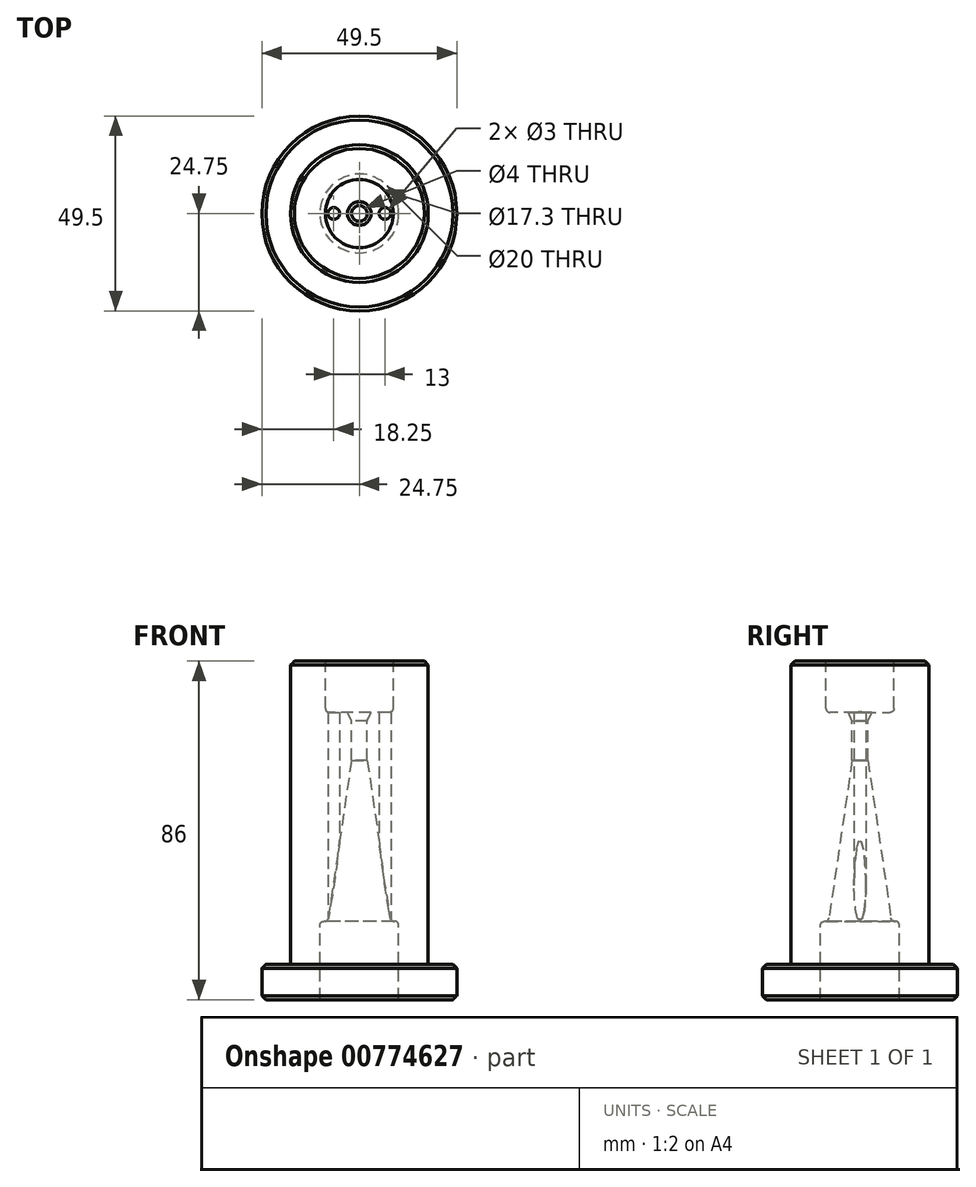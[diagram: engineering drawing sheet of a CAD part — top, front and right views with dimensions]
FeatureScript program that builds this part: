
annotation { "Feature Type Name" : "Feature", "Feature Type Description" : "" }
export const myFeature = defineFeature(function(context is Context, id is Id, definition is map)
    precondition{}
    {
        {
            var Q0;
            Q0=qCreatedBy(makeId("Front.planeOp"),FACE);
            var sketch = newSketch(context, id + "F0", { "sketchPlane" : qUnion([Q0])});
            skLineSegment(sketch, "E0", {"start": v(0, 0) * mm, "end": v(-10, 0) * mm});
            skLineSegment(sketch, "E1", {"start": v(-10, -2) * mm, "end": v(-10, -20) * mm});
            skLineSegment(sketch, "E2", {"start": v(-10, -20) * mm, "end": v(-24.75, -20) * mm});
            skLineSegment(sketch, "E3", {"start": v(-24.75, -20) * mm, "end": v(-24.75, -11) * mm});
            skLineSegment(sketch, "E4", {"start": v(-24.75, -11) * mm, "end": v(-18, -11) * mm});
            skLineSegment(sketch, "E5", {"start": v(-17.5, -10.5) * mm, "end": v(-17.5, 66) * mm});
            skLineSegment(sketch, "E6", {"start": v(-17.5, 66) * mm, "end": v(-8.65, 66) * mm});
            skLineSegment(sketch, "E7", {"start": v(-7.65, 53) * mm, "end": v(-3, 53) * mm});
            skLineSegment(sketch, "E8", {"start": v(-8.65, 54) * mm, "end": v(-8.65, 66) * mm});
            skLineSegment(sketch, "E9", {"start": v(-3, 53) * mm, "end": v(-2, 50.86) * mm});
            skLineSegment(sketch, "E10", {"start": v(-2, 50.86) * mm, "end": v(-2, 40.84) * mm});
            skPoint(sketch, "E11.orphan", {"position": v(0, 53) * mm});
            skLineSegment(sketch, "E12", {"start": v(-8, 0) * mm, "end": v(-8, 0) * mm});
            skLineSegment(sketch, "E13", {"start": v(-7.9, 0.72) * mm, "end": v(-2, 40.84) * mm});
            skPoint(sketch, "E14.end.orphan", {"position": v(0, 66) * mm});
            skPoint(sketch, "E15.visualSharp", {"position": v(-10, 0) * mm});
            skPoint(sketch, "E16.visualSharp", {"position": v(-8, 0) * mm});
            skArc(sketch, "E16.filletArc", {"start": v(-8.59, -0.09) * mm, "mid": v(-8.12, 0.22) * mm, "end": v(-7.9, 0.72) * mm});
            skLineSegment(sketch, "E17", {"start": v(-8.59, -0.09) * mm, "end": v(-8.94, -0.07) * mm});
            skLineSegment(sketch, "E18", {"start": v(-10, -2) * mm, "end": v(-10, -1.06) * mm});
            skArc(sketch, "E19.filletArc", {"start": v(-8.94, -0.07) * mm, "mid": v(-9.68, -0.34) * mm, "end": v(-10, -1.06) * mm});
            skPoint(sketch, "E20.visualSharp", {"position": v(-17.5, -11) * mm});
            skArc(sketch, "E20.filletArc", {"start": v(-18, -11) * mm, "mid": v(-17.65, -10.85) * mm, "end": v(-17.5, -10.5) * mm});
            skLineSegment(sketch, "E21", {"start": v(0, 75.07) * mm, "end": v(0, -45.35) * mm});
            skPoint(sketch, "E22.visualSharp", {"position": v(-8.65, 53) * mm});
            skArc(sketch, "E22.filletArc", {"start": v(-8.65, 54) * mm, "mid": v(-8.36, 53.3) * mm, "end": v(-7.65, 53) * mm});
            skSolve(sketch);
        }
        {
            var Q0;
            Q0=makeQuery(id+"F0.imprint","IMPRINT",FACE,{"disambiguationData":[TD([[makeQuery(id+"F0.imprint","IMPRINT",EDGE,{"derivedFrom":sQuery(id+"F0.wireOp",EDGE,"E1")}),-1.0]])]});
            var Q1;
            Q1=sQuery(id+"F0.wireOp",EDGE,"E21");
            revolve(context, id + "F1", {"surfaceOperationType" : NewSurfaceOperationType.NEW, "entities" : qUnion([Q0]), "axis" : qUnion([Q1]), "revolveType" : RevolveType.FULL});
        }
        {
            var Q0;
            Q0=makeQuery(id+"F1.opRevolve","SWEPT_EDGE",EDGE,{"disambiguationData":[OSD([sQuery(id+"F0.wireOp",EDGE,"E3"),sQuery(id+"F0.wireOp",EDGE,"E4")])]});
            var Q1;
            Q1=makeQuery(id+"F1.opRevolve","SWEPT_EDGE",EDGE,{"disambiguationData":[OSD([sQuery(id+"F0.wireOp",EDGE,"E5"),sQuery(id+"F0.wireOp",EDGE,"E6")])]});
            var Q2;
            Q2=makeQuery(id+"F1.opRevolve","SWEPT_EDGE",EDGE,{"disambiguationData":[OSD([sQuery(id+"F0.wireOp",EDGE,"E2"),sQuery(id+"F0.wireOp",EDGE,"E3")])]});
            chamfer(context, id + "F2", {"entities" : qUnion([Q0, Q1, Q2]), "width" : 1 * mm, "tangentPropagation" : true});
        }
        {
            var Q0;
            Q0=qCreatedBy(makeId("Top.planeOp"),FACE);
            var sketch = newSketch(context, id + "F3", { "sketchPlane" : qUnion([Q0])});
            skLineSegment(sketch, "E23", {"start": v(0, 0) * mm, "end": v(6.5, 0) * mm});
            skLineSegment(sketch, "E24", {"start": v(0, 0) * mm, "end": v(-6.5, 0) * mm});
            skCircle(sketch, "E25", {"center": v(-6.5, 0) * mm, "radius": 1.5 * mm});
            skCircle(sketch, "E26", {"center": v(6.5, 0) * mm, "radius": 1.5 * mm});
            skSolve(sketch);
        }
        {
            var Q0;
            Q0=makeQuery(id+"F3.imprint","IMPRINT",FACE,{"disambiguationData":[TD([[makeQuery(id+"F3.imprint","IMPRINT",EDGE,{"derivedFrom":sQuery(id+"F3.wireOp",EDGE,"E25")}),1.0]])]});
            var Q1;
            Q1=makeQuery(id+"F3.imprint","IMPRINT",FACE,{"disambiguationData":[TD([[makeQuery(id+"F3.imprint","IMPRINT",EDGE,{"derivedFrom":sQuery(id+"F3.wireOp",EDGE,"E26")}),1.0]])]});
            extrude(context, id + "F4", {"entities" : qUnion([Q0, Q1]), "operationType" : NewBodyOperationType.REMOVE, "depth" : 80 * mm, "offsetDistance" : 25 * mm});
        }
    });
